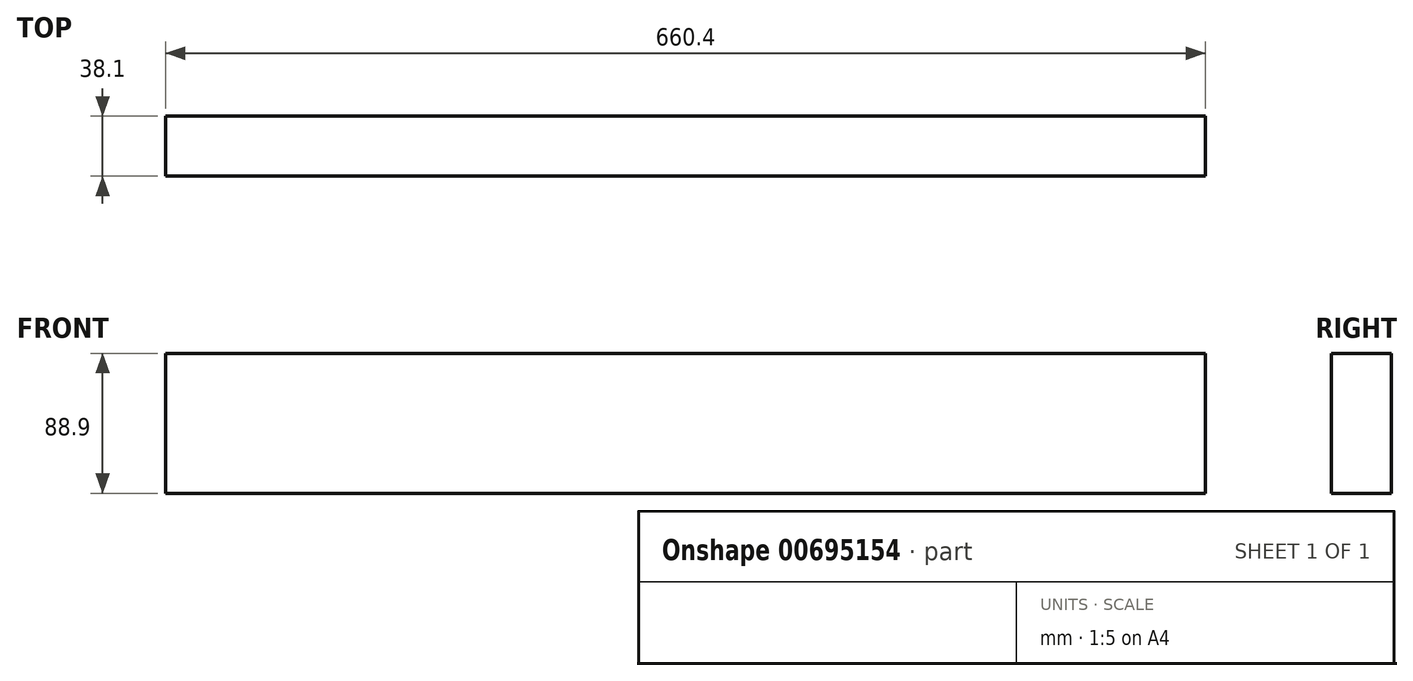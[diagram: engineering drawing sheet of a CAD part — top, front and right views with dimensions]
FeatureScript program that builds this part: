
annotation { "Feature Type Name" : "Feature", "Feature Type Description" : "" }
export const myFeature = defineFeature(function(context is Context, id is Id, definition is map)
    precondition{}
    {
        {
            var Q0;
            Q0=qCreatedBy(makeId("Right.planeOp"),FACE);
            var sketch = newSketch(context, id + "F0", { "sketchPlane" : qUnion([Q0])});
            skLineSegment(sketch, "E0.bottom", {"start": v(379.94, -162.52) * mm, "end": v(418.04, -162.52) * mm});
            skLineSegment(sketch, "E0.top", {"start": v(379.94, -251.42) * mm, "end": v(418.04, -251.42) * mm});
            skLineSegment(sketch, "E0.left", {"start": v(379.94, -162.52) * mm, "end": v(379.94, -251.42) * mm});
            skLineSegment(sketch, "E0.right", {"start": v(418.04, -162.52) * mm, "end": v(418.04, -251.42) * mm});
            skSolve(sketch);
        }
        {
            var Q0;
            Q0=makeQuery(id+"F0.imprint","IMPRINT",FACE,{"disambiguationData":[TD([[makeQuery(id+"F0.imprint","IMPRINT",EDGE,{"derivedFrom":sQuery(id+"F0.wireOp",EDGE,"E0.bottom")}),-1.0]])]});
            extrude(context, id + "F1", {"entities" : qUnion([Q0]), "depth" : 660.4 * mm, "offsetDistance" : 25.4 * mm});
        }
    });
